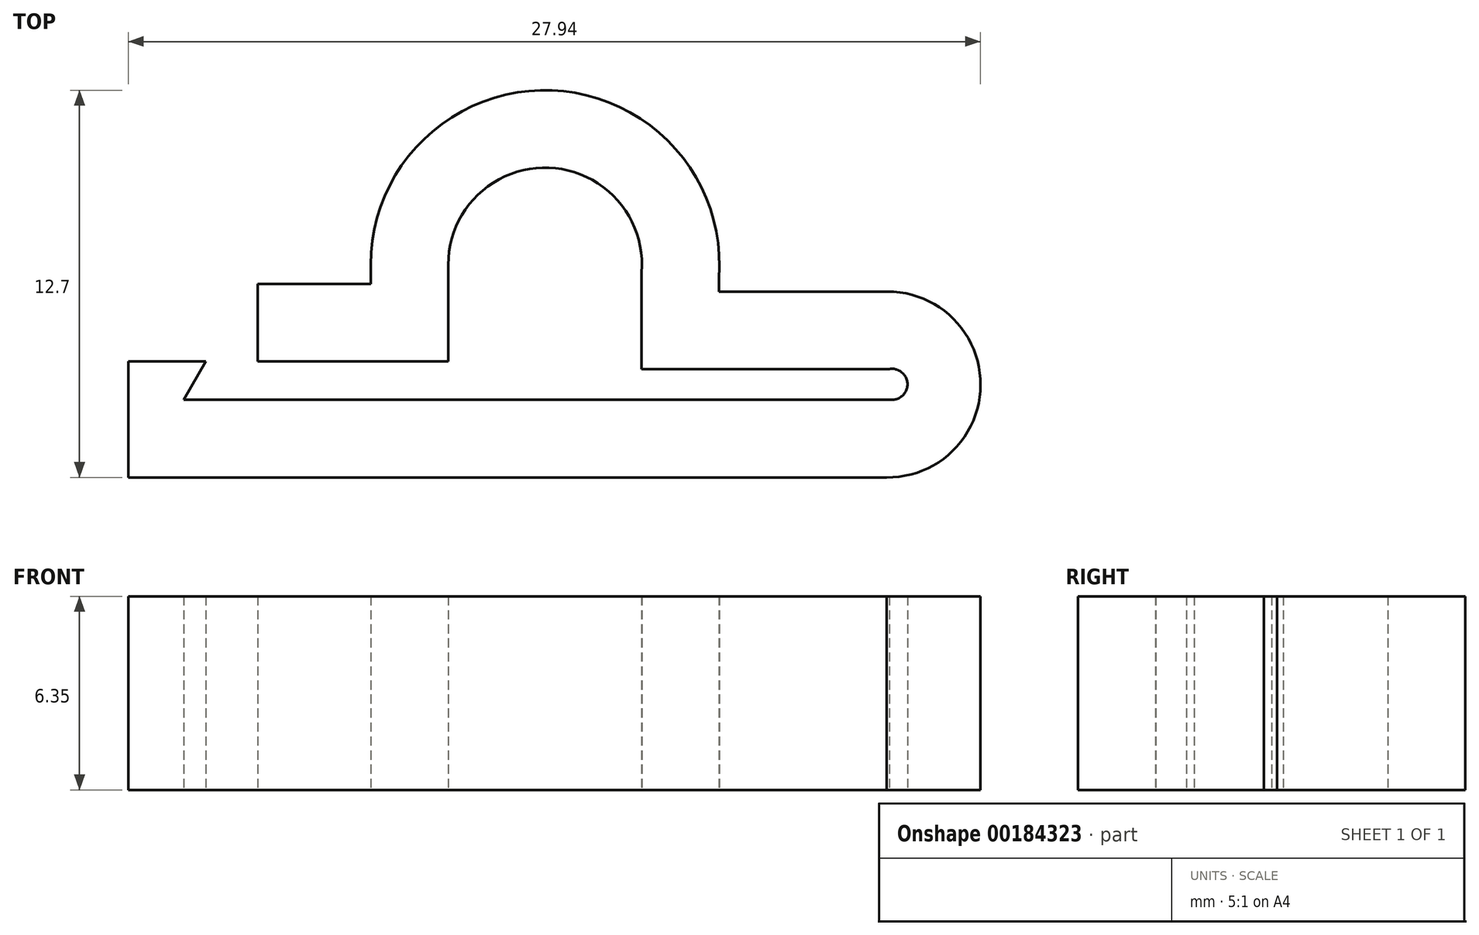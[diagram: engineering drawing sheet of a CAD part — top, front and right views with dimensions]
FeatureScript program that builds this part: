
annotation { "Feature Type Name" : "Feature", "Feature Type Description" : "" }
export const myFeature = defineFeature(function(context is Context, id is Id, definition is map)
    precondition{}
    {
        {
            var Q0;
            Q0=qCreatedBy(makeId("Top.planeOp"),FACE);
            var sketch = newSketch(context, id + "F0", { "sketchPlane" : qUnion([Q0])});
            skLineSegment(sketch, "E0", {"start": v(-26.66, 11.23) * mm, "end": v(-20.41, 11.23) * mm});
            skLineSegment(sketch, "E1", {"start": v(-14.07, 10.97) * mm, "end": v(-5.94, 10.97) * mm});
            skArc(sketch, "E2", {"start": v(-5.94, 9.97) * mm, "mid": v(-5.35, 10.47) * mm, "end": v(-5.94, 10.97) * mm});
            skLineSegment(sketch, "E3", {"start": v(-28.36, 11.23) * mm, "end": v(-30.9, 11.23) * mm});
            skLineSegment(sketch, "E4", {"start": v(-30.9, 11.23) * mm, "end": v(-30.9, 7.42) * mm});
            skLineSegment(sketch, "E5", {"start": v(-30.9, 7.42) * mm, "end": v(-6.04, 7.42) * mm});
            skLineSegment(sketch, "E6", {"start": v(-14.07, 10.97) * mm, "end": v(-14.07, 14.15) * mm});
            skLineSegment(sketch, "E7", {"start": v(-20.41, 11.23) * mm, "end": v(-20.41, 14.4) * mm});
            skArc(sketch, "E8", {"start": v(-14.07, 14.15) * mm, "mid": v(-17.1, 17.58) * mm, "end": v(-20.41, 14.4) * mm});
            skArc(sketch, "E9.0", {"start": v(-11.54, 13.95) * mm, "mid": v(-17, 20.11) * mm, "end": v(-22.95, 14.4) * mm});
            skLineSegment(sketch, "E10", {"start": v(-6, 16.2) * mm, "end": v(-6, 1.8) * mm, "construction": true});
            skLineSegment(sketch, "E11", {"start": v(-6, 13.51) * mm, "end": v(-11.54, 13.51) * mm});
            skLineSegment(sketch, "E12", {"start": v(-11.54, 13.95) * mm, "end": v(-11.54, 13.51) * mm});
            skArc(sketch, "E13", {"start": v(-6.04, 7.42) * mm, "mid": v(-2.96, 10.45) * mm, "end": v(-6, 13.51) * mm});
            skLineSegment(sketch, "E14", {"start": v(-26.66, 13.77) * mm, "end": v(-22.95, 13.77) * mm});
            skLineSegment(sketch, "E15", {"start": v(-22.95, 14.4) * mm, "end": v(-22.95, 13.77) * mm});
            skLineSegment(sketch, "E16", {"start": v(-26.66, 13.77) * mm, "end": v(-26.66, 11.23) * mm});
            skLineSegment(sketch, "E17", {"start": v(-28.36, 11.23) * mm, "end": v(-29.08, 9.97) * mm});
            skLineSegment(sketch, "E18", {"start": v(-5.94, 9.97) * mm, "end": v(-29.08, 9.97) * mm});
            skSolve(sketch);
        }
        {
            var Q0;
            Q0 = qSketchRegion(id + "F0", true);
            extrude(context, id + "F1", {"entities" : qUnion([Q0]), "depth" : 6.35 * mm});
        }
    });
